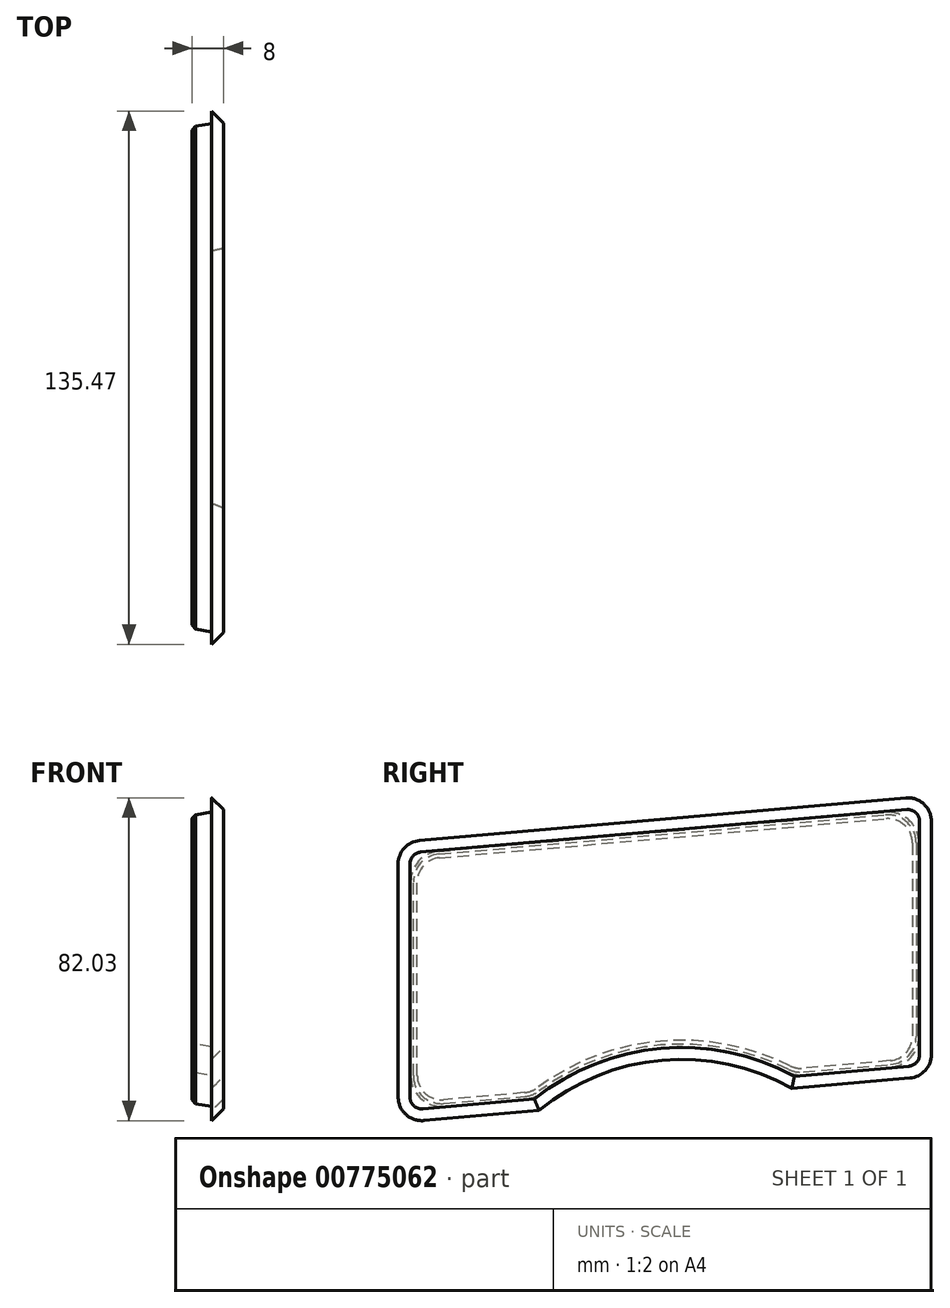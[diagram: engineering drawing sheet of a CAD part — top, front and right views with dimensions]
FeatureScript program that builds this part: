
annotation { "Feature Type Name" : "Feature", "Feature Type Description" : "" }
export const myFeature = defineFeature(function(context is Context, id is Id, definition is map)
    precondition{}
    {
        {
            var Q0;
            Q0=qCreatedBy(makeId("Right.planeOp"),FACE);
            var sketch = newSketch(context, id + "F0", { "sketchPlane" : qUnion([Q0])});
            skLineSegment(sketch, "E0", {"start": v(-76.69, -19.97) * mm, "end": v(-76.69, 55.32) * mm});
            skLineSegment(sketch, "E1", {"start": v(-76.69, 55.32) * mm, "end": v(62.78, 67.52) * mm});
            skLineSegment(sketch, "E2", {"start": v(62.78, 67.52) * mm, "end": v(62.78, -7.77) * mm});
            skArc(sketch, "E3", {"start": v(24.9, -11.08) * mm, "mid": v(-7.48, -3.87) * mm, "end": v(-38.11, -16.6) * mm});
            skLineSegment(sketch, "E4", {"start": v(-76.69, -19.97) * mm, "end": v(-38.11, -16.6) * mm});
            skPoint(sketch, "E5.orphan", {"position": v(48.77, -39.25) * mm});
            skPoint(sketch, "E6.orphan", {"position": v(62.78, -39.25) * mm});
            skLineSegment(sketch, "E7.trimOffspring", {"start": v(24.9, -11.08) * mm, "end": v(62.78, -7.77) * mm});
            skLineSegment(sketch, "E8.0", {"start": v(-71.69, -14.51) * mm, "end": v(-71.69, 50.74) * mm});
            skLineSegment(sketch, "E8.1", {"start": v(57.78, 62.06) * mm, "end": v(57.78, -3.18) * mm});
            skLineSegment(sketch, "E8.2", {"start": v(26, -5.97) * mm, "end": v(57.78, -3.18) * mm});
            skLineSegment(sketch, "E8.3", {"start": v(-71.69, 50.74) * mm, "end": v(57.78, 62.06) * mm});
            skArc(sketch, "E8.4", {"start": v(26, -5.97) * mm, "mid": v(-7.92, 1.1) * mm, "end": v(-40.09, -11.75) * mm});
            skLineSegment(sketch, "E8.5", {"start": v(-71.69, -14.51) * mm, "end": v(-40.09, -11.75) * mm});
            skSolve(sketch);
        }
        {
            var Q0;
            Q0=makeQuery(id+"F0.imprint","IMPRINT",FACE,{"disambiguationData":[TD([[makeQuery(id+"F0.imprint","IMPRINT",EDGE,{"derivedFrom":sQuery(id+"F0.wireOp",EDGE,"E0")}),-1.0]])]});
            var Q1;
            Q1=makeQuery(id+"F0.imprint","IMPRINT",FACE,{"disambiguationData":[TD([[makeQuery(id+"F0.imprint","IMPRINT",EDGE,{"derivedFrom":sQuery(id+"F0.wireOp",EDGE,"E8.0")}),-1.0]])]});
            extrude(context, id + "F1", {"entities" : qUnion([Q0, Q1]), "oppositeDirection" : true, "depth" : 3 * mm, "offsetDistance" : 25 * mm});
        }
        {
            var Q0;
            Q0=makeQuery(id+"F0.imprint","IMPRINT",FACE,{"disambiguationData":[TD([[makeQuery(id+"F0.imprint","IMPRINT",EDGE,{"derivedFrom":sQuery(id+"F0.wireOp",EDGE,"E8.0")}),-1.0]])]});
            extrude(context, id + "F2", {"entities" : qUnion([Q0]), "operationType" : NewBodyOperationType.ADD, "oppositeDirection" : true, "depth" : 8 * mm, "offsetDistance" : 25 * mm});
        }
        {
            var Q0;
            Q0=makeQuery(id+"F2.opExtrude","SWEPT_EDGE",EDGE,{"disambiguationData":[OSD([sQuery(id+"F0.wireOp",EDGE,"E8.1"),sQuery(id+"F0.wireOp",EDGE,"E8.3")])]});
            var Q1;
            Q1=makeQuery(id+"F2.opExtrude","SWEPT_EDGE",EDGE,{"disambiguationData":[OSD([sQuery(id+"F0.wireOp",EDGE,"E8.0"),sQuery(id+"F0.wireOp",EDGE,"E8.3")])]});
            var Q2;
            Q2=makeQuery(id+"F2.opExtrude","SWEPT_EDGE",EDGE,{"disambiguationData":[OSD([sQuery(id+"F0.wireOp",EDGE,"E8.0"),sQuery(id+"F0.wireOp",EDGE,"E8.5")])]});
            var Q3;
            Q3=makeQuery(id+"F2.opExtrude","SWEPT_EDGE",EDGE,{"disambiguationData":[OSD([sQuery(id+"F0.wireOp",EDGE,"E8.4"),sQuery(id+"F0.wireOp",EDGE,"E8.5")])]});
            var Q4;
            Q4=makeQuery(id+"F2.opExtrude","SWEPT_EDGE",EDGE,{"disambiguationData":[OSD([sQuery(id+"F0.wireOp",EDGE,"E8.2"),sQuery(id+"F0.wireOp",EDGE,"E8.4")])]});
            var Q5;
            Q5=makeQuery(id+"F2.opExtrude","SWEPT_EDGE",EDGE,{"disambiguationData":[OSD([sQuery(id+"F0.wireOp",EDGE,"E8.1"),sQuery(id+"F0.wireOp",EDGE,"E8.2")])]});
            var Q6;
            Q6=makeQuery(id+"F1.opExtrude","SWEPT_EDGE",EDGE,{"disambiguationData":[OSD([sQuery(id+"F0.wireOp",EDGE,"E0"),sQuery(id+"F0.wireOp",EDGE,"E1")])]});
            var Q7;
            Q7=makeQuery(id+"F1.opExtrude","SWEPT_EDGE",EDGE,{"disambiguationData":[OSD([sQuery(id+"F0.wireOp",EDGE,"E0"),sQuery(id+"F0.wireOp",EDGE,"E4")])]});
            var Q8;
            Q8=makeQuery(id+"F1.opExtrude","SWEPT_EDGE",EDGE,{"disambiguationData":[OSD([sQuery(id+"F0.wireOp",EDGE,"E2"),sQuery(id+"F0.wireOp",EDGE,"E7.trimOffspring")])]});
            var Q9;
            Q9=makeQuery(id+"F1.opExtrude","SWEPT_EDGE",EDGE,{"disambiguationData":[OSD([sQuery(id+"F0.wireOp",EDGE,"E1"),sQuery(id+"F0.wireOp",EDGE,"E2")])]});
            fillet(context, id + "F3", {"entities" : qUnion([Q0, Q1, Q2, Q3, Q4, Q5, Q6, Q7, Q8, Q9]), "radius" : 8 * mm, "tangentPropagation" : true, "allowEdgeOverflow" : false});
        }
        {
            var Q0;
            Q0=makeQuery(id+"F2.opExtrude","CAP_EDGE",EDGE,{"disambiguationData":[OSD([sQuery(id+"F0.wireOp",EDGE,"E8.3")])],"isStart":false});
            chamfer(context, id + "F4", {"entities" : qUnion([Q0]), "chamferType" : ChamferType.TWO_OFFSETS, "width1" : 1 * mm, "oppositeDirection" : false, "width2" : 6 * mm, "tangentPropagation" : true});
        }
        {
            var Q0;
            {var subQ0=sQuery(id+"F0.wireOp",EDGE,"E8.3");Q0=makeQuery(id+"F4.opChamfer","BLEND_EDGE",EDGE,{"blendedFrom":[makeQuery(id+"F2.opExtrude","CAP_EDGE",EDGE,{"disambiguationData":[OSD([subQ0])],"isStart":false}),makeQuery(id+"F2.opExtrude","CAP_FACE",FACE,{"disambiguationData":[OSD([sQuery(id+"F0.wireOp",EDGE,"E8.0"),sQuery(id+"F0.wireOp",EDGE,"E8.1"),sQuery(id+"F0.wireOp",EDGE,"E8.2"),subQ0,sQuery(id+"F0.wireOp",EDGE,"E8.4"),sQuery(id+"F0.wireOp",EDGE,"E8.5")])],"isStart":false})],"blendedInto":[makeQuery(id+"F2.opExtrude","CAP_FACE",FACE,{"disambiguationData":[OSD([sQuery(id+"F0.wireOp",EDGE,"E8.0"),sQuery(id+"F0.wireOp",EDGE,"E8.1"),sQuery(id+"F0.wireOp",EDGE,"E8.2"),subQ0,sQuery(id+"F0.wireOp",EDGE,"E8.4"),sQuery(id+"F0.wireOp",EDGE,"E8.5")])],"isStart":false})]});}
            chamfer(context, id + "F5", {"entities" : qUnion([Q0]), "width" : 1 * mm, "tangentPropagation" : true});
        }
        {
            var Q0;
            Q0=makeQuery(id+"F1.opExtrude","CAP_EDGE",EDGE,{"disambiguationData":[OSD([sQuery(id+"F0.wireOp",EDGE,"E1")])],"isStart":true});
            var Q1;
            Q1=makeQuery(id+"F1.opExtrude","CAP_EDGE",EDGE,{"disambiguationData":[OSD([sQuery(id+"F0.wireOp",EDGE,"E3")])],"isStart":true});
            chamfer(context, id + "F6", {"entities" : qUnion([Q0, Q1]), "width" : 5 * mm, "tangentPropagation" : true});
        }
    });
